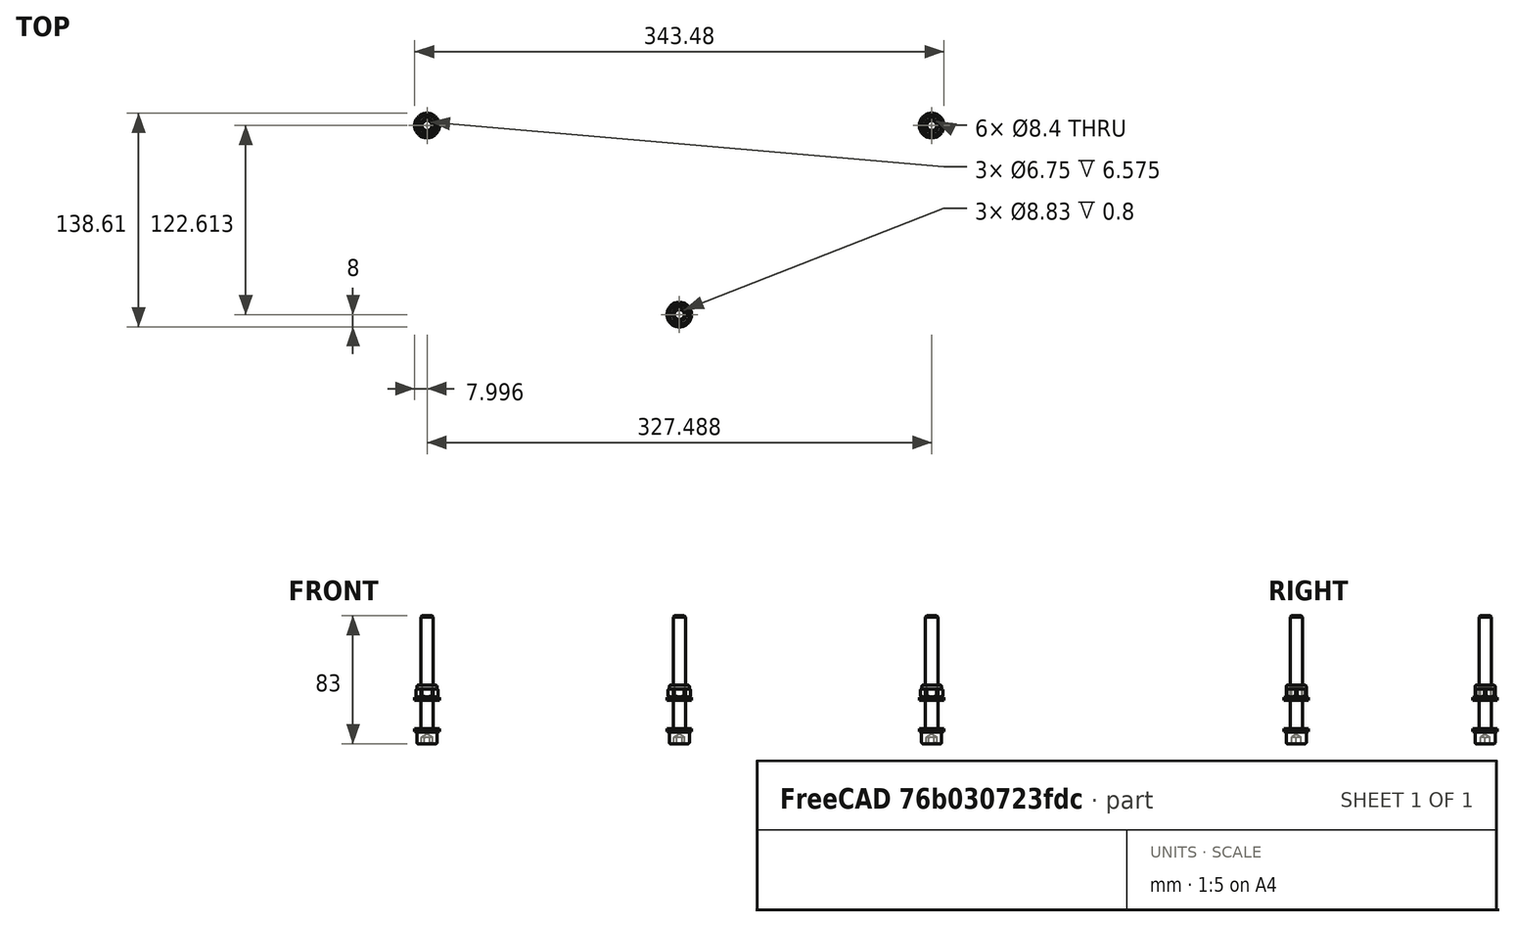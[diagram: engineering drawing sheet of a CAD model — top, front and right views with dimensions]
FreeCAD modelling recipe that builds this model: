
FCSTD DOCUMENT  (FreeCAD 0.20R29410 (Git))
Label: ASM_Platform
License: All rights reserved
LicenseURL: http://en.wikipedia.org/wiki/All_rights_reserved
objects: Part::FeaturePython×13, App::DocumentObjectGroup×4, App::Link×4, PartDesign::CoordinateSystem×2, App::FeaturePython×1, App::Part×1
note: 15 computed .brp shape members not serialized (recipe doc carries the construction recipe); baked Part::Feature solids carry a one-line shape summary decoded from their .brp
EXTERNAL_REF file=ComputerPlatform.FCStd obj=LCS_Origin
EXTERNAL_REF file=ComputerPlatform.FCStd obj=Assembly
EXTERNAL_REF file=ASM_GantrySkate.FCStd obj=LCS_Origin
EXTERNAL_REF file=Params.FCStd obj=Spreadsheet
EXTERNAL_REF file=ASM_GantrySkate.FCStd obj=Assembly
EXTERNAL_REF file=../../../../../AppData/Local/Temp/FreeCAD/Cache/FreeCAD_Doc_e326eb17-bc0b-4666-96ed-1d71e9908fb8_da39a3_8856 obj=LCS_Origin
EXTERNAL_REF file=../../../../../AppData/Local/Temp/FreeCAD/Cache/FreeCAD_Doc_e326eb17-bc0b-4666-96ed-1d71e9908fb8_da39a3_8856 obj=Assembly
EXTERNAL_REF file=AlExtrusion2040.FCStd obj=Assembly
EXTERNAL_REF file=ASM_ExtensionDriver.FCStd obj=LCS_Origin
EXTERNAL_REF file=ASM_ExtensionDriver.FCStd obj=Assembly
EXTERNAL_REF file=ComputerPlatform.FCStd obj=LCS_TopPivot
EXTERNAL_REF file=ComputerPlatform.FCStd obj=Pad
EXTERNAL_REF file=ComputerPlatform.FCStd obj=Body

FEATURE [App::DocumentObjectGroup] Parts
FEATURE [PartDesign::CoordinateSystem] LCS_Origin
  AttacherType = Attacher::AttachEngine3D
  MapMode = 2
  Support = -> [X_Axis]
FEATURE [App::FeaturePython] Variables  # WARN: FeaturePython — macro-defined, semantics opaque (R4)
  Type = App::PropertyContainer
FEATURE [App::DocumentObjectGroup] Constraints
FEATURE [App::DocumentObjectGroup] Configurations
FEATURE [App::Link] ComputerPlatform
  AttachedBy = #LCS_Origin
  AttachedTo = Parent Assembly#LCS_Origin
  LinkedObject = -> <external ComputerPlatform.FCStd>#Assembly
  SolverId = Asm4EE
  expr: Placement = LCS_Origin.Placement * AttachmentOffset * ComputerPlatform#LCS_Origin.Placement ^ -1
FEATURE [App::Link] ASM_GantrySkate  label="ASM_GantrySkate001"
  AttachedBy = #LCS_Origin
  AttachedTo = ComputerPlatform#LCS_Origin
  AttachmentOffset = pos=(20,-367,0) rot=(0,1,0;3.14159rad)
  LinkPlacement = pos=(20,-367,0) rot=(0,1,0;3.14159rad)
  LinkedObject = -> <external ASM_GantrySkate.FCStd>#Assembly
  Placement = pos=(20,-367,0) rot=(0,1,0;3.14159rad)
  SolverId = Asm4EE
  expr: .AttachmentOffset.Base.x = <<Params>>#<<Params>>.ExtensionArmCenterOffset
  expr: Placement = ComputerPlatform.Placement * ComputerPlatform#LCS_Origin.Placement * AttachmentOffset * ASM_GantrySkate#LCS_Origin.Placement ^ -1
FEATURE [App::Link] ASM_GantrySkate001  label="ASM_GantrySkate002"
  AttachedBy = #LCS_Origin
  AttachedTo = ComputerPlatform#LCS_Origin
  AttachmentOffset = pos=(20,192,0) rot=(0,1,0;3.14159rad)
  LinkPlacement = pos=(20,192,0) rot=(0,1,0;3.14159rad)
  LinkedObject = -> <external ASM_GantrySkate.FCStd>#Assembly
  Placement = pos=(20,192,0) rot=(0,1,0;3.14159rad)
  SolverId = Asm4EE
  expr: .AttachmentOffset.Base.x = <<Params>>#<<Params>>.ExtensionArmCenterOffset
  expr: Placement = ComputerPlatform.Placement * ComputerPlatform#LCS_Origin.Placement * AttachmentOffset * ASM_GantrySkate#LCS_Origin.Placement ^ -1
FEATURE [Part::FeaturePython] AlExtrusion2040_var  # link proxy (typed FeaturePython)
  AttachedBy = #LCS_Origin
  AttachedTo = ASM_GantrySkate#LCS_Origin
  AttachmentOffset = pos=(0,-30,23.5) rot=(0.57735,-0.57735,-0.57735;4.18879rad)
  Length = 2000
  LinkedObject = -> <external ../../../../../AppData/Local/Temp/FreeCAD/Cache/FreeCAD_Doc_e326eb17-bc0b-4666-96ed-1d71e9908fb8_da39a3_8856>#Assembly
  Placement = pos=(20,-397,-23.5) rot=(-0.57735,-0.57735,-0.57735;2.0944rad)
  SolverId = Asm4EE
  SourceObject = -> <external AlExtrusion2040.FCStd>#Assembly
  expr: Placement = ASM_GantrySkate.Placement * ASM_GantrySkate#LCS_Origin.Placement * AttachmentOffset * varTmpDoc_2#LCS_Origin.Placement ^ -1
FEATURE [App::Link] ASM_ExtensionDriver
  AttachedBy = #LCS_Origin
  AttachedTo = ComputerPlatform#LCS_Origin
  AttachmentOffset = pos=(-16,-300,0) rot=(0.707107,0.707107,0;3.14159rad)
  LinkPlacement = pos=(-16,-300,0) rot=(0.707107,0.707107,0;3.14159rad)
  LinkedObject = -> <external ASM_ExtensionDriver.FCStd>#Assembly
  Placement = pos=(-16,-300,0) rot=(0.707107,0.707107,0;3.14159rad)
  SolverId = Asm4EE
  expr: Placement = ComputerPlatform.Placement * ComputerPlatform#LCS_Origin.Placement * AttachmentOffset * ASM_ExtensionDriver#LCS_Origin.Placement ^ -1
FEATURE [PartDesign::CoordinateSystem] ComputerPlatform_LCS_TopPivot
  AttachedBy = Origin
  AttacherType = Attacher::AttachEngine3D
  Placement = pos=(0,0,18.5) rot=(0,0,1;0rad)
  SolverId = Asm4EE
  expr: Placement = ComputerPlatform.Placement * ComputerPlatform#LCS_TopPivot.Placement
FEATURE [Part::FeaturePython] Washer  label="M8-Washer"  # Fasteners workbench fastener (typed FeaturePython)
  Placement = pos=(163.744,212.613,0) rot=(-1,0,0;3.14159rad)
  diameter = 8
  invert = true
  matchOuter = false
  offset = 0
  type = 3
FEATURE [Part::FeaturePython] Washer001  label="M8-Washer005"  # Fasteners workbench fastener (typed FeaturePython)
  Placement = pos=(-163.744,212.613,0) rot=(-1,0,0;3.14159rad)
  diameter = 8
  invert = true
  matchOuter = false
  offset = 0
  type = 3
FEATURE [Part::FeaturePython] Washer002  label="M8-Washer004"  # Fasteners workbench fastener (typed FeaturePython)
  Placement = pos=(0,90,0) rot=(-1,0,0;3.14159rad)
  baseObject = -> <external ComputerPlatform.FCStd>#Pad [Edge53]
  diameter = 8
  invert = true
  matchOuter = false
  offset = 0
  type = 3
FEATURE [Part::FeaturePython] Screw  label="M8x75-Screw"  # Fasteners workbench fastener (typed FeaturePython)
  Placement = pos=(0,90,-1.8) rot=(-1,0,0;3.14159rad)
  baseObject = -> Washer002 [Edge1]
  diameter = 8
  invert = false
  length = 15
  lengthCustom = 75
  matchOuter = true
  offset = 0
  thread = false
  type = 34
FEATURE [Part::FeaturePython] Screw001  label="M8x75-Screw001"  # Fasteners workbench fastener (typed FeaturePython)
  Placement = pos=(-163.744,212.613,-1.8) rot=(-1,0,0;3.14159rad)
  baseObject = -> Washer001 [Edge1]
  diameter = 8
  invert = false
  length = 15
  lengthCustom = 75
  matchOuter = true
  offset = 0
  thread = false
  type = 34
FEATURE [Part::FeaturePython] Screw002  label="M8x75-Screw002"  # Fasteners workbench fastener (typed FeaturePython)
  Placement = pos=(163.744,212.613,-1.8) rot=(-1,0,0;3.14159rad)
  baseObject = -> Washer [Edge1]
  diameter = 8
  invert = false
  length = 15
  lengthCustom = 75
  matchOuter = true
  offset = 0
  thread = false
  type = 34
FEATURE [Part::FeaturePython] Washer003  label="M8-Washer006"  # Fasteners workbench fastener (typed FeaturePython)
  Placement = pos=(0,90,18.5) rot=(0,0,1;0rad)
  baseObject = -> <external ComputerPlatform.FCStd>#Body [Edge54]
  diameter = 8
  invert = false
  matchOuter = true
  offset = 0
  type = 3
FEATURE [Part::FeaturePython] Washer004  label="M8-Washer007"  # Fasteners workbench fastener (typed FeaturePython)
  Placement = pos=(163.744,212.613,18.5) rot=(0,0,1;0rad)
  baseObject = -> <external ComputerPlatform.FCStd>#Body [Edge60]
  diameter = 8
  invert = false
  matchOuter = true
  offset = 0
  type = 3
FEATURE [Part::FeaturePython] Washer005  label="M8-Washer008"  # Fasteners workbench fastener (typed FeaturePython)
  Placement = pos=(-163.744,212.613,18.5) rot=(0,0,1;0rad)
  baseObject = -> <external ComputerPlatform.FCStd>#Body [Edge57]
  diameter = 8
  invert = false
  matchOuter = true
  offset = 0
  type = 3
FEATURE [Part::FeaturePython] Nut  label="M8-Nut"  # Fasteners workbench fastener (typed FeaturePython)
  Placement = pos=(0,90,20.3) rot=(0,0,1;0rad)
  baseObject = -> Washer003 [Edge1]
  diameter = 6
  invert = false
  matchOuter = true
  offset = 0
  thread = false
  type = 5
FEATURE [Part::FeaturePython] Nut001  label="M8-Nut001"  # Fasteners workbench fastener (typed FeaturePython)
  Placement = pos=(163.744,212.613,20.3) rot=(0,0,1;0rad)
  baseObject = -> Washer004 [Edge1]
  diameter = 6
  invert = false
  matchOuter = true
  offset = 0
  thread = false
  type = 5
FEATURE [Part::FeaturePython] Nut002  label="M8-Nut002"  # Fasteners workbench fastener (typed FeaturePython)
  Placement = pos=(-163.744,212.613,20.3) rot=(0,0,1;0rad)
  baseObject = -> Washer005 [Edge1]
  diameter = 6
  invert = false
  matchOuter = true
  offset = 0
  thread = false
  type = 5
FEATURE [App::DocumentObjectGroup] Fasteners
  Group = -> [Washer,Washer001,Washer002,Screw,Screw001,Screw002,Washer003,Washer004,Washer005,Nut,Nut001,Nut002]
FEATURE [App::Part] Assembly
  AssemblyType = Part::Link
  Group = -> [LCS_Origin,Variables,Constraints,Configurations,ComputerPlatform,ASM_GantrySkate,ASM_GantrySkate001,AlExtrusion2040_var,ASM_ExtensionDriver,ComputerPlatform_LCS_TopPivot,Fasteners,Washer,Washer001,Washer002,Screw,Screw001,Screw002,Washer003,Washer004,Washer005,Nut,Nut001,Nut002]
  Origin = -> Origin
  Type = Assembly

RESOLVED EXTERNAL PARTS (link-assembly join: the EXTERNAL_REF files above that resolve inside this repo's crawl, each included once):
---- part ASM_ExtensionDriver.FCStd = doc fcstd_aab446da4b41 ----
FCSTD DOCUMENT  (FreeCAD 0.20R29410 (Git))
Label: ASM_ExtensionDriver
License: All rights reserved
LicenseURL: http://en.wikipedia.org/wiki/All_rights_reserved
objects: App::Link×5, App::DocumentObjectGroup×3, PartDesign::CoordinateSystem×1, App::FeaturePython×1, App::Part×1
note: 1 computed .brp shape members not serialized (recipe doc carries the construction recipe); baked Part::Feature solids carry a one-line shape summary decoded from their .brp
EXTERNAL_REF file=ASM_Stepper.FCStd obj=LCS_Origin
EXTERNAL_REF file=ASM_Stepper.FCStd obj=Assembly
EXTERNAL_REF file=ASM_Stepper.FCStd obj=Stepper_LCS_mount
EXTERNAL_REF file=SerpentinePlate.FCStd obj=LCS_Origin
EXTERNAL_REF file=SerpentinePlate.FCStd obj=Assembly
EXTERNAL_REF file=TimingPulleyGT2.FCStd obj=LCS_Origin
EXTERNAL_REF file=TimingPulleyGT2.FCStd obj=Assembly
EXTERNAL_REF file=SerpentinePlate.FCStd obj=LCS_idler1
EXTERNAL_REF file=SmoothIdlerPulleyGT2.FCStd obj=LCS_Origin
EXTERNAL_REF file=SmoothIdlerPulleyGT2.FCStd obj=Assembly
EXTERNAL_REF file=SerpentinePlate.FCStd obj=LCS_idler2

FEATURE [App::DocumentObjectGroup] Parts
FEATURE [PartDesign::CoordinateSystem] LCS_Origin
  AttacherType = Attacher::AttachEngine3D
  MapMode = 2
  Support = -> [X_Axis]
FEATURE [App::FeaturePython] Variables  # WARN: FeaturePython — macro-defined, semantics opaque (R4)
  Type = App::PropertyContainer
FEATURE [App::DocumentObjectGroup] Constraints
FEATURE [App::DocumentObjectGroup] Configurations
FEATURE [App::Link] ASM_Stepper
  AttachedBy = #LCS_Origin
  AttachedTo = Parent Assembly#LCS_Origin
  LinkedObject = -> <external ASM_Stepper.FCStd>#Assembly
  SolverId = Asm4EE
  expr: Placement = LCS_Origin.Placement * AttachmentOffset * ASM_Stepper#LCS_Origin.Placement ^ -1
FEATURE [App::Link] SerpentinePlate
  AttachedBy = #LCS_Origin
  AttachedTo = ASM_Stepper#Stepper_LCS_mount
  AttachmentOffset = pos=(0,0,-3) rot=(-1,0,0;3.14159rad)
  LinkPlacement = pos=(0,-6.7e-15,30) rot=(-1,0,0;1.5708rad)
  LinkedObject = -> <external SerpentinePlate.FCStd>#Assembly
  Placement = pos=(0,-6.7e-15,30) rot=(-1,0,0;1.5708rad)
  SolverId = Asm4EE
  expr: Placement = ASM_Stepper.Placement * ASM_Stepper#Stepper_LCS_mount.Placement * AttachmentOffset * SerpentinePlate#LCS_Origin.Placement ^ -1
FEATURE [App::Link] TimingPulleyGT2
  AttachedBy = #LCS_Origin
  AttachedTo = ASM_Stepper#Stepper_LCS_mount
  AttachmentOffset = pos=(0,0,-26) rot=(0,0,1;0rad)
  LinkPlacement = pos=(0,23,30) rot=(1,0,0;1.5708rad)
  LinkedObject = -> <external TimingPulleyGT2.FCStd>#Assembly
  Placement = pos=(0,23,30) rot=(1,0,0;1.5708rad)
  SolverId = Asm4EE
  expr: Placement = ASM_Stepper.Placement * ASM_Stepper#Stepper_LCS_mount.Placement * AttachmentOffset * TimingPulleyGT2#LCS_Origin.Placement ^ -1
FEATURE [App::Link] SmoothIdlerPulleyGT2
  AttachedBy = #LCS_Origin
  AttachedTo = SerpentinePlate#LCS_idler1
  AttachmentOffset = pos=(0,0,1) rot=(0,0,1;0rad)
  LinkPlacement = pos=(16.3,8,37.5) rot=(-1,0,0;1.5708rad)
  LinkedObject = -> <external SmoothIdlerPulleyGT2.FCStd>#Assembly
  Placement = pos=(16.3,8,37.5) rot=(-1,0,0;1.5708rad)
  SolverId = Asm4EE
  expr: Placement = SerpentinePlate.Placement * SerpentinePlate#LCS_idler1.Placement * AttachmentOffset * SmoothIdlerPulleyGT2#LCS_Origin.Placement ^ -1
FEATURE [App::Link] SmoothIdlerPulleyGT003
  AttachedBy = #LCS_Origin
  AttachedTo = SerpentinePlate#LCS_idler2
  AttachmentOffset = pos=(0,0,1) rot=(0,0,1;0rad)
  LinkPlacement = pos=(-16.3,8,37.5) rot=(-1,0,0;1.5708rad)
  LinkedObject = -> <external SmoothIdlerPulleyGT2.FCStd>#Assembly
  Placement = pos=(-16.3,8,37.5) rot=(-1,0,0;1.5708rad)
  SolverId = Asm4EE
  expr: Placement = SerpentinePlate.Placement * SerpentinePlate#LCS_idler2.Placement * AttachmentOffset * SmoothIdlerPulleyGT2#LCS_Origin.Placement ^ -1
FEATURE [App::Part] Assembly
  AssemblyType = Part::Link
  Group = -> [LCS_Origin,Variables,Constraints,Configurations,ASM_Stepper,SerpentinePlate,TimingPulleyGT2,SmoothIdlerPulleyGT2,SmoothIdlerPulleyGT003]
  Origin = -> Origin
  Type = Assembly
---- part ASM_GantrySkate.FCStd = doc fcstd_a700c4be92d5 ----
FCSTD DOCUMENT  (FreeCAD 0.20R29410 (Git))
Label: ASM_GantrySkate
License: All rights reserved
LicenseURL: http://en.wikipedia.org/wiki/All_rights_reserved
objects: App::Link×5, App::DocumentObjectGroup×3, PartDesign::CoordinateSystem×1, App::FeaturePython×1, App::Part×1
note: 1 computed .brp shape members not serialized (recipe doc carries the construction recipe); baked Part::Feature solids carry a one-line shape summary decoded from their .brp
EXTERNAL_REF file=GantryBracket.FCStd obj=LCS_Origin
EXTERNAL_REF file=GantryBracket.FCStd obj=Assembly
EXTERNAL_REF file=GantryBracket.FCStd obj=LCS_wheel1
EXTERNAL_REF file=GantryWheel.FCStd obj=LCS_Origin
EXTERNAL_REF file=GantryWheel.FCStd obj=Assembly
EXTERNAL_REF file=GantryBracket.FCStd obj=LCS_wheel2
EXTERNAL_REF file=GantryBracket.FCStd obj=LCS_wheel3
EXTERNAL_REF file=GantryBracket.FCStd obj=LCS_wheel4

FEATURE [App::DocumentObjectGroup] Parts
FEATURE [PartDesign::CoordinateSystem] LCS_Origin
  AttacherType = Attacher::AttachEngine3D
  MapMode = 2
  Support = -> [X_Axis]
FEATURE [App::FeaturePython] Variables  # WARN: FeaturePython — macro-defined, semantics opaque (R4)
  Type = App::PropertyContainer
FEATURE [App::DocumentObjectGroup] Constraints
FEATURE [App::DocumentObjectGroup] Configurations
FEATURE [App::Link] GantryBracket
  AttachedBy = #LCS_Origin
  AttachedTo = Parent Assembly#LCS_Origin
  LinkedObject = -> <external GantryBracket.FCStd>#Assembly
  SolverId = Asm4EE
  expr: Placement = LCS_Origin.Placement * AttachmentOffset * GantryBracket#LCS_Origin.Placement ^ -1
FEATURE [App::Link] GantryWheel
  AttachedBy = #LCS_Origin
  AttachedTo = GantryBracket#LCS_wheel1
  LinkPlacement = pos=(-19.85,20,3) rot=(0,0,1;1.5708rad)
  LinkedObject = -> <external GantryWheel.FCStd>#Assembly
  Placement = pos=(-19.85,20,3) rot=(0,0,1;1.5708rad)
  SolverId = Asm4EE
  expr: Placement = GantryBracket.Placement * GantryBracket#LCS_wheel1.Placement * AttachmentOffset * GantryWheel#LCS_Origin.Placement ^ -1
FEATURE [App::Link] GantryWheel001
  AttachedBy = #LCS_Origin
  AttachedTo = GantryBracket#LCS_wheel2
  LinkPlacement = pos=(19.85,20,3) rot=(0,0,1;1.5708rad)
  LinkedObject = -> <external GantryWheel.FCStd>#Assembly
  Placement = pos=(19.85,20,3) rot=(0,0,1;1.5708rad)
  SolverId = Asm4EE
  expr: Placement = GantryBracket.Placement * GantryBracket#LCS_wheel2.Placement * AttachmentOffset * GantryWheel#LCS_Origin.Placement ^ -1
FEATURE [App::Link] GantryWheel002
  AttachedBy = #LCS_Origin
  AttachedTo = GantryBracket#LCS_wheel3
  LinkPlacement = pos=(-19.85,-20,3) rot=(0,0,1;1.5708rad)
  LinkedObject = -> <external GantryWheel.FCStd>#Assembly
  Placement = pos=(-19.85,-20,3) rot=(0,0,1;1.5708rad)
  SolverId = Asm4EE
  expr: Placement = GantryBracket.Placement * GantryBracket#LCS_wheel3.Placement * AttachmentOffset * GantryWheel#LCS_Origin.Placement ^ -1
FEATURE [App::Link] GantryWheel003
  AttachedBy = #LCS_Origin
  AttachedTo = GantryBracket#LCS_wheel4
  LinkPlacement = pos=(19.85,-20,3) rot=(0,0,1;1.5708rad)
  LinkedObject = -> <external GantryWheel.FCStd>#Assembly
  Placement = pos=(19.85,-20,3) rot=(0,0,1;1.5708rad)
  SolverId = Asm4EE
  expr: Placement = GantryBracket.Placement * GantryBracket#LCS_wheel4.Placement * AttachmentOffset * GantryWheel#LCS_Origin.Placement ^ -1
FEATURE [App::Part] Assembly
  AssemblyType = Part::Link
  Group = -> [LCS_Origin,Variables,Constraints,Configurations,GantryBracket,GantryWheel,GantryWheel001,GantryWheel002,GantryWheel003]
  Origin = -> Origin
  Type = Assembly
---- part AlExtrusion2040.FCStd = doc fcstd_975970cbc615 ----
FCSTD DOCUMENT  (FreeCAD 0.20R29410 (Git))
Label: AlExtrusion2040
License: All rights reserved
LicenseURL: http://en.wikipedia.org/wiki/All_rights_reserved
objects: App::DocumentObjectGroup×3, PartDesign::Mirrored×2, PartDesign::CoordinateSystem×1, App::FeaturePython×1, Sketcher::SketchObject×1, PartDesign::Pad×1, PartDesign::MultiTransform×1, PartDesign::Body×1, App::Part×1
note: 8 computed .brp shape members not serialized (recipe doc carries the construction recipe); baked Part::Feature solids carry a one-line shape summary decoded from their .brp

FEATURE [App::DocumentObjectGroup] Parts
FEATURE [PartDesign::CoordinateSystem] LCS_Origin
  AttacherType = Attacher::AttachEngine3D
  MapMode = 2
  Support = -> [X_Axis]
FEATURE [App::FeaturePython] Variables  # WARN: FeaturePython — macro-defined, semantics opaque (R4)
  Length = 100
  Type = App::PropertyContainer
FEATURE [App::DocumentObjectGroup] Constraints
FEATURE [App::DocumentObjectGroup] Configurations
FEATURE [Sketcher::SketchObject] Sketch
  FullyConstrained = true
  MapMode = 5
  Support = -> [XY_Plane001]
  sketch-geometry (30):
    g0: LineSegment StartX=0 StartY=10 StartZ=0 EndX=5.1 EndY=10 EndZ=0
    g1: LineSegment StartX=5.1 StartY=10 StartZ=0 EndX=6.9 EndY=8.2 EndZ=0
    g2: LineSegment StartX=6.9 StartY=8.2 StartZ=0 EndX=4.5 EndY=8.2 EndZ=0
    g3: LineSegment StartX=4.5 StartY=8.2 StartZ=0 EndX=4.5 EndY=6.56066 EndZ=0
    g4: LineSegment StartX=4.5 StartY=6.56066 StartZ=0 EndX=7.06066 EndY=4 EndZ=0
    g5: LineSegment StartX=7.06066 StartY=4 StartZ=0 EndX=12.9393 EndY=4 EndZ=0
    g6: LineSegment StartX=12.9393 StartY=4 StartZ=0 EndX=15.5 EndY=6.56066 EndZ=0
    g7: LineSegment StartX=15.5 StartY=6.56066 StartZ=0 EndX=15.5 EndY=8.2 EndZ=0
    g8: LineSegment StartX=15.5 StartY=8.2 StartZ=0 EndX=13.1 EndY=8.2 EndZ=0
    g9: LineSegment StartX=13.1 StartY=8.2 StartZ=0 EndX=14.9 EndY=10 EndZ=0
    g10: LineSegment StartX=14.9 StartY=10 StartZ=0 EndX=20 EndY=10 EndZ=0
    g11: LineSegment StartX=20 StartY=10 StartZ=0 EndX=20 EndY=4.9 EndZ=0
    g12: LineSegment StartX=20 StartY=4.9 StartZ=0 EndX=18.2 EndY=3.1 EndZ=0
    g13: LineSegment StartX=18.2 StartY=3.1 StartZ=0 EndX=18.2 EndY=5.5 EndZ=0
    g14: LineSegment StartX=18.2 StartY=5.5 StartZ=0 EndX=16.5607 EndY=5.5 EndZ=0
    g15: LineSegment StartX=16.5607 StartY=5.5 StartZ=0 EndX=14 EndY=2.93934 EndZ=0
    g16: LineSegment StartX=14 StartY=2.93934 StartZ=0 EndX=14 EndY=0 EndZ=0
    g17: LineSegment StartX=14 StartY=2.93934 StartZ=0 EndX=12.9393 EndY=4 EndZ=0
    g18: LineSegment StartX=14 StartY=0 StartZ=0 EndX=12.1 EndY=0 EndZ=0
    g19: ArcOfCircle CenterX=10 CenterY=0 CenterZ=0 NormalX=0 NormalY=0 NormalZ=1 AngleXU=0 Radius=2.1 StartAngle=0 EndAngle=3.14159
    g20: LineSegment StartX=7.9 StartY=3e-16 StartZ=0 EndX=6 EndY=3e-16 EndZ=0
    g21: LineSegment StartX=6 StartY=3e-16 StartZ=0 EndX=6 EndY=2.93934 EndZ=0
    g22: LineSegment StartX=6 StartY=2.93934 StartZ=0 EndX=3 EndY=5.93934 EndZ=0
    g23: LineSegment StartX=3 StartY=5.93934 StartZ=0 EndX=3 EndY=8.2 EndZ=0
    g24: LineSegment StartX=3 StartY=8.2 StartZ=0 EndX=0 EndY=8.2 EndZ=0
    g25: LineSegment StartX=0 StartY=10 StartZ=0 EndX=0 EndY=8.2 EndZ=0
    g26: LineSegment StartX=7.06066 StartY=4 StartZ=0 EndX=6 EndY=2.93934 EndZ=0
    g27: LineSegment StartX=3 StartY=8.2 StartZ=0 EndX=4.5 EndY=8.2 EndZ=0
    g28: GeomPoint X=10 Y=8.2 Z=0
    g29: LineSegment StartX=10 StartY=8.2 StartZ=0 EndX=10 EndY=0 EndZ=0
  constraints (85):
    c: PointOnObject(g0,g-2)
    c: Coincident(g0,g1)
    c: Coincident(g1,g2)
    c: Coincident(g2,g3)
    c: Coincident(g3,g4)
    c: Coincident(g4,g5)
    c: Horizontal(g5)
    c: Coincident(g5,g6)
    c: Coincident(g6,g7)
    c: Vertical(g7)
    c: Coincident(g7,g8)
    c: Horizontal(g8)
    c: Coincident(g8,g9)
    c: Coincident(g9,g10)
    c: Horizontal(g10)
    c: Coincident(g10,g11)
    c: Vertical(g11)
    c: Coincident(g11,g12)
    c: Coincident(g12,g13)
    c: Coincident(g13,g14)
    c: Coincident(g14,g15)
    c: Coincident(g15,g16)
    c: PointOnObject(g16,g-1)
    c: Vertical(g16)
    c: Horizontal(g14)
    c: Vertical(g13)
    c: Angle(g15,g-1) = 2.35619
    c: Parallel(g6,g15)
    c: Perpendicular(g6,g4)
    c: Vertical(g3)
    c: Horizontal(g2)
    c: Parallel(g1,g4)
    c: Horizontal(g0)
    c: Coincident(g17,g15)
    c: Coincident(g17,g5)
    c: Perpendicular(g15,g17)
    c: Distance(g17) = 1.5
    c: Coincident(g16,g18)
    c: PointOnObject(g18,g-1)
    c: PointOnObject(g19,g-1)
    c: Coincident(g19,g18)
    c: PointOnObject(g19,g-1)
    c: Coincident(g19,g20)
    c: Coincident(g20,g21)
    c: Vertical(g21)
    c: Coincident(g21,g22)
    c: Coincident(g22,g23)
    c: Vertical(g23)
    c: Coincident(g23,g24)
    c: PointOnObject(g24,g-2)
    c: Horizontal(g24)
    c: Coincident(g25,g0)
    c: Coincident(g25,g24)
    c: Parallel(g22,g4)
    c: Coincident(g26,g4)
    c: Coincident(g26,g21)
    c: Perpendicular(g22,g26)
    c: Equal(g26,g17)
    c: Equal(g7,g3)
    c: Coincident(g27,g23)
    c: Coincident(g27,g2)
    c: Horizontal(g27)
    c: DistanceY(g25,g25) = 1.8
    c: DistanceX(g-1,g19) = 10
    c: Horizontal(g20)
    c: Diameter(g19) = 4.2
    c: Equal(g27,g26)
    c: Parallel(g12,g15)
    c: Parallel(g9,g6)
    c: PointOnObject(g8,g2)
    c: PointOnObject(g9,g0)
    c: DistanceY(g-1,g0) = 10
    c: DistanceX(g2,g7) = 11
    c: DistanceX(g1,g8) = 6.2
    c: Equal(g14,g7)
    c: Equal(g13,g8)
    c: DistanceX(g0,g10) = 20
    c: Equal(g10,g11)
    c: Equal(g12,g9)
    c: Symmetric(g8,g1,g28)
    c: Coincident(g29,g28)
    c: Coincident(g29,g19)
    c: Vertical(g29)
    c: Equal(g18,g20)
    c: DistanceX(g20,g16) = 8
FEATURE [PartDesign::Pad] Pad
  Direction = (0,0,1)
  Length = 100
  Length2 = 10
  Profile = -> Sketch
  ReferenceAxis = -> Sketch [N_Axis]
  Type = 0
  expr: Length = <<Variables>>.Length
FEATURE [PartDesign::Mirrored] Mirrored
  MirrorPlane = -> Sketch [V_Axis]
FEATURE [PartDesign::Mirrored] Mirrored001
  MirrorPlane = -> Sketch [H_Axis]
FEATURE [PartDesign::MultiTransform] MultiTransform
  BaseFeature = -> Pad
  Originals = -> [Pad]
  Transformations = -> [Mirrored,Mirrored001]
FEATURE [PartDesign::Body] Body
  Group = -> [Sketch,Pad,MultiTransform,Mirrored,Mirrored001]
  Origin = -> Origin001
  Tip = -> MultiTransform
FEATURE [App::Part] Assembly
  AssemblyType = Part::Link
  Group = -> [LCS_Origin,Variables,Constraints,Configurations,Body]
  Origin = -> Origin
  Type = Assembly
---- part ComputerPlatform.FCStd = doc fcstd_b58720267baf ----
FCSTD DOCUMENT  (FreeCAD 0.20R29410 (Git))
Label: ComputerPlatform
License: All rights reserved
LicenseURL: http://en.wikipedia.org/wiki/All_rights_reserved
objects: App::DocumentObjectGroup×3, PartDesign::CoordinateSystem×2, Sketcher::SketchObject×1, PartDesign::Pad×1, PartDesign::Body×1, App::FeaturePython×1, App::Part×1
note: 6 computed .brp shape members not serialized (recipe doc carries the construction recipe); baked Part::Feature solids carry a one-line shape summary decoded from their .brp
EXTERNAL_REF file=DrivePlatform.FCStd obj=Sketch
EXTERNAL_REF file=Params.FCStd obj=Spreadsheet

FEATURE [Sketcher::SketchObject] Sketch
  FullyConstrained = true
  MapMode = 5
  Support = -> [XY_Plane]
  expr: Constraints[57] = <<DrivePlatform>>#<<Sketch>>.Constraints.DriveAdjSpacingX
  expr: Constraints[58] = <<DrivePlatform>>#<<Sketch>>.Constraints.DriveAdjSpacingY
  expr: Constraints[59] = <<Params>>#<<Params>>.DriveAdjMiddleOffset
  sketch-geometry (30):
    g0: LineSegment StartX=-220 StartY=6.1e-15 StartZ=0 EndX=-220 EndY=-400 EndZ=0
    g1: LineSegment StartX=-214 StartY=-406 StartZ=0 EndX=214 EndY=-406 EndZ=0
    g2: LineSegment StartX=220 StartY=-400 StartZ=0 EndX=220 EndY=0 EndZ=0
    g3: Circle CenterX=0 CenterY=0 CenterZ=0 NormalX=0 NormalY=0 NormalZ=1 AngleXU=0 Radius=25
    g4: Circle CenterX=51 CenterY=51 CenterZ=0 NormalX=0 NormalY=0 NormalZ=1 AngleXU=0 Radius=6.5
    g5: Circle CenterX=-51 CenterY=51 CenterZ=0 NormalX=0 NormalY=0 NormalZ=1 AngleXU=0 Radius=6.5
    g6: Circle CenterX=-51 CenterY=-51 CenterZ=0 NormalX=0 NormalY=0 NormalZ=1 AngleXU=0 Radius=6.5
    g7: Circle CenterX=51 CenterY=-51 CenterZ=0 NormalX=0 NormalY=0 NormalZ=1 AngleXU=0 Radius=6.5
    g8: LineSegment StartX=51 StartY=51 StartZ=0 EndX=51 EndY=-51 EndZ=0
    g9: LineSegment StartX=51 StartY=51 StartZ=0 EndX=-51 EndY=51 EndZ=0
    g10: ArcOfCircle CenterX=214 CenterY=-400 CenterZ=0 NormalX=0 NormalY=0 NormalZ=1 AngleXU=0 Radius=6 StartAngle=4.71239 EndAngle=6.28319
    g11: GeomPoint X=220 Y=-406 Z=0
    g12: ArcOfCircle CenterX=-214 CenterY=-400 CenterZ=0 NormalX=0 NormalY=0 NormalZ=1 AngleXU=0 Radius=6 StartAngle=3.14159 EndAngle=4.71239
    g13: GeomPoint X=-220 Y=-406 Z=0
    g14: ArcOfCircle CenterX=-170 CenterY=0 CenterZ=0 NormalX=0 NormalY=0 NormalZ=1 AngleXU=0 Radius=50 StartAngle=2.94211 EndAngle=3.14159
    g15: ArcOfCircle CenterX=170 CenterY=0 CenterZ=0 NormalX=0 NormalY=0 NormalZ=1 AngleXU=0 Radius=50 StartAngle=0 EndAngle=0.199484
    g16: GeomPoint X=0 Y=-406 Z=0
    g17: LineSegment StartX=-219.008 StartY=9.90816 StartZ=0 EndX=-177.466 EndY=215.387 EndZ=0
    g18: LineSegment StartX=219.008 StartY=9.90816 StartZ=0 EndX=177.466 EndY=215.387 EndZ=0
    g19: Circle CenterX=0 CenterY=90 CenterZ=0 NormalX=0 NormalY=0 NormalZ=1 AngleXU=0 Radius=4.1
    g20: Circle CenterX=163.744 CenterY=212.613 CenterZ=0 NormalX=0 NormalY=0 NormalZ=1 AngleXU=0 Radius=4.1
    g21: Circle CenterX=-163.744 CenterY=212.613 CenterZ=0 NormalX=0 NormalY=0 NormalZ=1 AngleXU=0 Radius=4.1
    g22: LineSegment StartX=-163.744 StartY=226.613 StartZ=0 EndX=163.744 EndY=226.613 EndZ=0
    g23: GeomPoint X=0 Y=226.613 Z=0
    g24: LineSegment StartX=-163.744 StartY=212.613 StartZ=0 EndX=0 EndY=212.613 EndZ=0
    g25: LineSegment StartX=0 StartY=212.613 StartZ=0 EndX=163.744 EndY=212.613 EndZ=0
    g26: ArcOfCircle CenterX=163.744 CenterY=212.613 CenterZ=0 NormalX=0 NormalY=0 NormalZ=1 AngleXU=0 Radius=14 StartAngle=0.199484 EndAngle=1.5708
    g27: GeomPoint X=175.197 Y=226.613 Z=0
    g28: ArcOfCircle CenterX=-163.744 CenterY=212.613 CenterZ=0 NormalX=0 NormalY=0 NormalZ=1 AngleXU=0 Radius=14 StartAngle=1.5708 EndAngle=2.94211
    g29: GeomPoint X=-175.197 Y=226.613 Z=0
  constraints (70):
    c: Vertical(g0)
    c: Horizontal(g1)
    c: Vertical(g2)
    c: DistanceX(g13,g11) = 440
    c: Diameter(g3) = 50
    c: Coincident(g8,g4)
    c: Coincident(g8,g7)
    c: Coincident(g9,g4)
    c: Coincident(g9,g5)
    c: Equal(g9,g8)
    c: Vertical(g8)
    c: Horizontal(g9)
    c: Equal(g4,g5)
    c: Equal(g5,g6)
    c: Equal(g6,g7)
    c: Diameter(g4) = 13
    c: DistanceY(g8,g8) = 102
    c: PointOnObject(g11,g2)
    c: PointOnObject(g11,g1)
    c: Tangent(g2,g10) = -1.5708
    c: Tangent(g1,g10) = -1.5708
    c: PointOnObject(g13,g0)
    c: PointOnObject(g13,g1)
    c: Tangent(g0,g12) = -1.5708
    c: Tangent(g1,g12) = -1.5708
    c: Equal(g12,g10)
    c: Radius(g10) = 6
    c: Coincident(g3,g-1)
    c: Symmetric(g7,g5,g3)
    c: Symmetric(g6,g4,g3)
    c: PointOnObject(g2,g-1)
    c: PointOnObject(g0,g-1)
    c: PointOnObject(g14,g-1)
    c: Coincident(g14,g0)
    c: PointOnObject(g15,g-1)
    c: Coincident(g15,g2)
    c: PointOnObject(g16,g-2)
    c: Symmetric(g1,g1,g16)
    c: DistanceY(g0,g0) = 400
    c: Equal(g14,g15)
    c: Radius(g15) = 50
    c: Tangent(g18,g15) = -1.5708
    c: Tangent(g17,g14) = 1.5708
    c: PointOnObject(g19,g-2)
    c: Equal(g21,g20)
    c: Equal(g20,g19)
    c: Diameter(g19) = 8.2
    c: Horizontal(g22)
    c: Symmetric(g29,g27,g23)
    c: PointOnObject(g23,g-2)
    c: Coincident(g24,g21)
    c: Horizontal(g24)
    c: Coincident(g25,g24)
    c: Horizontal(g25)
    c: Coincident(g25,g20)
    c: Equal(g24,g25)
    c: PointOnObject(g24,g-2)
    c: DistanceX(g21,g20) = 327.488
    c: DistanceY(g19,g21) = 122.613
    c: DistanceY(g3,g19) = 90
    c: PointOnObject(g27,g18)
    c: PointOnObject(g27,g22)
    c: Tangent(g18,g26) = -1.5708
    c: Tangent(g22,g26) = 1.5708
    c: PointOnObject(g29,g22)
    c: Tangent(g22,g28) = 1.5708
    c: Tangent(g17,g28) = 1.5708
    c: Coincident(g28,g21)
    c: Coincident(g26,g20)
    c: Radius(g26) = 14
FEATURE [PartDesign::Pad] Pad
  Direction = (0,0,1)
  Length = 18.5
  Length2 = 10
  Profile = -> Sketch
  ReferenceAxis = -> Sketch [N_Axis]
  Type = 0
  expr: Length = <<Params>>#<<Params>>.PlywoodThickness
FEATURE [PartDesign::Body] Body
  Group = -> [Sketch,Pad]
  Origin = -> Origin
  Tip = -> Pad
FEATURE [App::DocumentObjectGroup] Parts
FEATURE [PartDesign::CoordinateSystem] LCS_Origin
  AttacherType = Attacher::AttachEngine3D
  MapMode = 2
  Support = -> [X_Axis001]
FEATURE [App::FeaturePython] Variables  # WARN: FeaturePython — macro-defined, semantics opaque (R4)
  Type = App::PropertyContainer
FEATURE [App::DocumentObjectGroup] Constraints
FEATURE [App::DocumentObjectGroup] Configurations
FEATURE [PartDesign::CoordinateSystem] LCS_TopPivot
  AttacherType = Attacher::AttachEngine3D
  AttachmentOffset = pos=(0,0,18.5) rot=(0,0,1;0rad)
  MapMode = 2
  Placement = pos=(0,0,18.5) rot=(0,0,1;0rad)
  Support = -> [LCS_Origin]
  expr: .AttachmentOffset.Base.z = <<Pad>>.Length
FEATURE [App::Part] Assembly
  AssemblyType = Part::Link
  Group = -> [LCS_Origin,Variables,Constraints,Configurations,Body,LCS_TopPivot]
  Origin = -> Origin001
  Type = Assembly
---- part Params.FCStd = doc fcstd_d7bdad1026f8 ----
FCSTD DOCUMENT  (FreeCAD 0.20R29410 (Git))
Label: Params
License: All rights reserved
LicenseURL: http://en.wikipedia.org/wiki/All_rights_reserved
objects: Spreadsheet::Sheet×1

FEATURE [Spreadsheet::Sheet] Spreadsheet  label="Params"
  cells = A1=DriveWheelWidth; B1(DriveWheelWidth)=10; D1=PlywoodThickness; E1(PlywoodThickness)=18.5; A2=DriveWheelMajorDiameter; B2(DriveWheelMajorDiameter)=52; D2=ExtensionArmCenterOffset; E2(ExtensionArmCenterOffset)=20; A3=DriveWheelCrown; B3(DriveWheelCrown)=2; A4=DriveWheelTireThickness; B4(DriveWheelTireThickness)=3; A6=DriveUnitAngle; B6(DriveUnitAngle)=30; A7=DriveRadius; B7(DriveRadius)=280; A8=DriveAdjMiddleOffset; B8(DriveAdjMiddleOffset)=90
